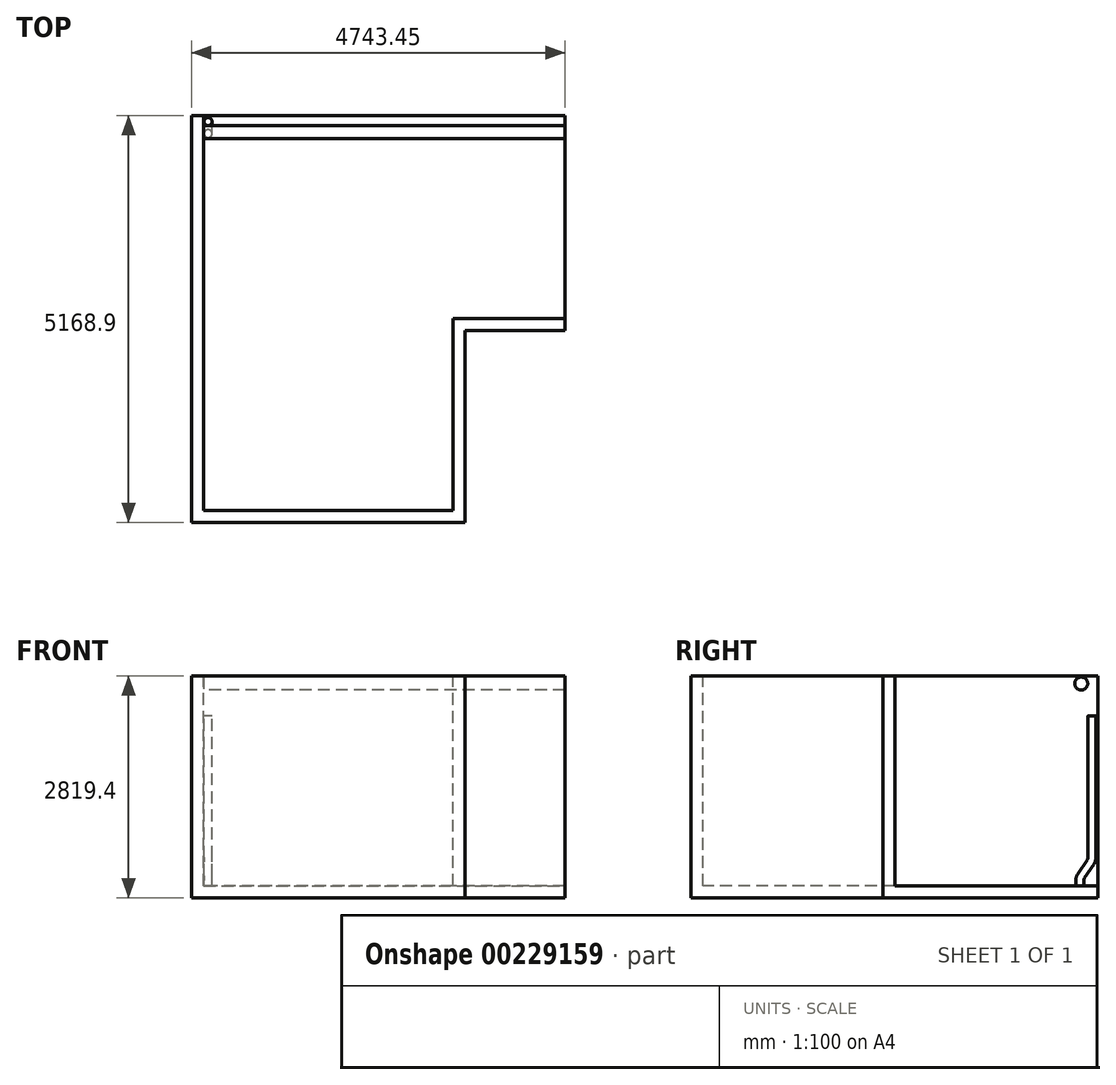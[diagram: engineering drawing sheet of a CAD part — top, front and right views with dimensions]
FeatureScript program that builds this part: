
annotation { "Feature Type Name" : "Feature", "Feature Type Description" : "" }
export const myFeature = defineFeature(function(context is Context, id is Id, definition is map)
    precondition{}
    {
        {
            var Q0;
            Q0=qCreatedBy(makeId("Top.planeOp"),FACE);
            var sketch = newSketch(context, id + "F0", { "sketchPlane" : qUnion([Q0])});
            skLineSegment(sketch, "E0", {"start": v(0, 0) * mm, "end": v(4584.7, 0) * mm});
            skLineSegment(sketch, "E1", {"start": v(4584.7, 0) * mm, "end": v(4584.7, -2578.1) * mm});
            skLineSegment(sketch, "E2", {"start": v(4584.7, -2578.1) * mm, "end": v(3162.3, -2578.1) * mm});
            skLineSegment(sketch, "E3", {"start": v(3162.3, -2578.1) * mm, "end": v(3162.3, -5016.5) * mm});
            skLineSegment(sketch, "E4", {"start": v(3162.3, -5016.5) * mm, "end": v(0, -5016.5) * mm});
            skLineSegment(sketch, "E5", {"start": v(0, 0) * mm, "end": v(0, -5016.5) * mm});
            skLineSegment(sketch, "E6", {"start": v(0, 0) * mm, "end": v(0, -228.6) * mm});
            skLineSegment(sketch, "E7", {"start": v(0, -228.6) * mm, "end": v(50.8, -228.6) * mm});
            skCircle(sketch, "E8", {"center": v(50.8, -228.6) * mm, "radius": 50.8 * mm});
            skSolve(sketch);
        }
        {
            var Q0;
            Q0=qCreatedBy(makeId("Right.planeOp"),FACE);
            var sketch = newSketch(context, id + "F1", { "sketchPlane" : qUnion([Q0])});
            skLineSegment(sketch, "E9", {"start": v(0, 0) * mm, "end": v(-228.6, 0) * mm});
            skLineSegment(sketch, "E10", {"start": v(-228.6, 0) * mm, "end": v(-228.6, 70.84) * mm});
            skLineSegment(sketch, "E11", {"start": v(-76.2, 360.96) * mm, "end": v(-76.2, 2159) * mm});
            skLineSegment(sketch, "E12", {"start": v(-93.26, 304.6) * mm, "end": v(-211.54, 127.2) * mm});
            skPoint(sketch, "E13.visualSharp", {"position": v(-228.6, 101.6) * mm});
            skArc(sketch, "E13.filletArc", {"start": v(-211.54, 127.2) * mm, "mid": v(-224.24, 100.28) * mm, "end": v(-228.6, 70.84) * mm});
            skPoint(sketch, "E14.visualSharp", {"position": v(-76.2, 330.2) * mm});
            skArc(sketch, "E14.filletArc", {"start": v(-93.26, 304.6) * mm, "mid": v(-80.56, 331.52) * mm, "end": v(-76.2, 360.96) * mm});
            skCircle(sketch, "E15", {"center": v(-211.54, 2570.42) * mm, "radius": 82.55 * mm});
            skLineSegment(sketch, "E16", {"start": v(-228.6, 0) * mm, "end": v(-211.54, 2570.42) * mm});
            skSolve(sketch);
        }
        {
            var Q0;
            Q0=makeQuery(id+"F0.imprint","IMPRINT",FACE,{"disambiguationData":[TD([[makeQuery(id+"F0.imprint","IMPRINT",EDGE,{"derivedFrom":sQuery(id+"F0.wireOp",EDGE,"E8")}),1.0]])]});
            var Q1;
            Q1=sQuery(id+"F1.wireOp",EDGE,"E10");
            var Q2;
            Q2=sQuery(id+"F1.wireOp",EDGE,"E13.filletArc");
            var Q3;
            Q3=sQuery(id+"F1.wireOp",EDGE,"E12");
            var Q4;
            Q4=sQuery(id+"F1.wireOp",EDGE,"E14.filletArc");
            var Q5;
            Q5=sQuery(id+"F1.wireOp",EDGE,"E11");
            sweep(context, id + "F2", {"profiles" : qUnion([Q0]), "path" : qUnion([Q1, Q2, Q3, Q4, Q5])});
        }
        {
            var Q0;
            Q0=makeQuery(id+"F0.imprint","IMPRINT",FACE,{"disambiguationData":[TD([[makeQuery(id+"F0.imprint","IMPRINT",EDGE,{"derivedFrom":sQuery(id+"F0.wireOp",EDGE,"E8")}),1.0]])]});
            var Q1;
            Q1=makeQuery(id+"F0.imprint","IMPRINT",FACE,{"disambiguationData":[TD([[makeQuery(id+"F0.imprint","IMPRINT",EDGE,{"derivedFrom":sQuery(id+"F0.wireOp",EDGE,"E0")}),-1.0]])]});
            extrude(context, id + "F3", {"entities" : qUnion([Q0, Q1]), "operationType" : NewBodyOperationType.ADD, "oppositeDirection" : true, "depth" : 152.4 * mm});
        }
        {
            var Q0;
            Q0=makeQuery(id+"F3.opExtrude","SWEPT_FACE",FACE,{"disambiguationData":[OSD([sQuery(id+"F0.wireOp",EDGE,"E5"),sQuery(id+"F0.wireOp",EDGE,"E6")])]});
            extrude(context, id + "F4", {"entities" : qUnion([Q0]), "operationType" : NewBodyOperationType.ADD, "depth" : 6.35 * mm});
        }
        {
            var Q0;
            Q0=makeQuery(id+"F4.opExtrude","CAP_FACE",FACE,{"disambiguationData":[OSD([sQuery(id+"F0.wireOp",EDGE,"E5"),sQuery(id+"F0.wireOp",EDGE,"E6")])],"isStart":false});
            extrude(context, id + "F5", {"entities" : qUnion([Q0]), "depth" : 152.4 * mm});
        }
        {
            var Q0;
            {var subQ1=sQuery(id+"F0.wireOp",EDGE,"E6");var subQ2=sQuery(id+"F0.wireOp",EDGE,"E5");var subQ3=sQuery(id+"F0.wireOp",EDGE,"E4");var subQ4=sQuery(id+"F0.wireOp",EDGE,"E0");var subQ7=makeQuery(id+"F3.opExtrude","CAP_EDGE",EDGE,{"disambiguationData":[OSD([subQ2,subQ1])],"isStart":true});Q0=makeQuery(id+"F5.opExtrude","SWEPT_FACE",FACE,{"disambiguationData":[OSD([subQ2,subQ1]),TDD([makeQuery(id+"F4.opExtrude","CAP_EDGE",EDGE,{"disambiguationData":[OSD([subQ2,subQ1]),TDD([makeQuery(id+"F3.boolean.opBoolean","SPLIT",EDGE,{"disambiguationData":[TD([makeQuery(id+"F3.opExtrude","SWEPT_FACE",FACE,{"disambiguationData":[OSD([subQ4])]})])],"derivedFrom":subQ7}),makeQuery(id+"F3.boolean.opBoolean","SPLIT",EDGE,{"disambiguationData":[TD([makeQuery(id+"F3.opExtrude","SWEPT_FACE",FACE,{"disambiguationData":[OSD([subQ3])]})])],"derivedFrom":subQ7})])],"isStart":false})])]});}
            extrude(context, id + "F6", {"entities" : qUnion([Q0]), "operationType" : NewBodyOperationType.ADD, "depth" : 2667 * mm});
        }
        {
            var Q0;
            Q0=makeQuery(id+"F1.imprint","IMPRINT",FACE,{"disambiguationData":[TD([[makeQuery(id+"F1.imprint","IMPRINT",EDGE,{"derivedFrom":sQuery(id+"F1.wireOp",EDGE,"E15")}),1.0]])]});
            var Q1;
            Q1=sQuery(id+"F0.wireOp",VERTEX,"E1.start");
            extrude(context, id + "F7", {"entities" : qUnion([Q0]), "endBound" : BoundingType.UP_TO_VERTEX, "endBoundEntityVertex" : qUnion([Q1]), "depth" : 6477 * mm});
        }
        {
            var Q0;
            Q0=makeQuery(id+"F1.imprint","IMPRINT",FACE,{"disambiguationData":[TD([[makeQuery(id+"F1.imprint","IMPRINT",EDGE,{"derivedFrom":sQuery(id+"F1.wireOp",EDGE,"E15")}),1.0]])]});
            extrude(context, id + "F8", {"entities" : qUnion([Q0]), "operationType" : NewBodyOperationType.ADD, "oppositeDirection" : true, "depth" : 152.4 * mm});
        }
        {
            var Q0;
            {var subQ0=sQuery(id+"F0.wireOp",EDGE,"E5");var subQ1=sQuery(id+"F0.wireOp",EDGE,"E4");Q0=makeQuery(id+"F6.boolean.opBoolean","MERGE",FACE,{"derivedFrom":[makeQuery(id+"F4.boolean.opBoolean","MERGE",FACE,{"derivedFrom":[makeQuery(id+"F3.opExtrude","SWEPT_FACE",FACE,{"disambiguationData":[OSD([subQ1])]}),makeQuery(id+"F4.opExtrude","SWEPT_FACE",FACE,{"disambiguationData":[OSD([subQ1,subQ0])]})]}),makeQuery(id+"F5.opExtrude","SWEPT_FACE",FACE,{"disambiguationData":[OSD([subQ1,subQ0])]}),makeQuery(id+"F6.opExtrude","SWEPT_FACE",FACE,{"disambiguationData":[OSD([subQ1,subQ0])]})]});}
            extrude(context, id + "F9", {"entities" : qUnion([Q0]), "depth" : 152.4 * mm});
        }
        {
            var Q0;
            {var subQ0=sQuery(id+"F0.wireOp",EDGE,"E5");var subQ1=sQuery(id+"F0.wireOp",EDGE,"E4");Q0=makeQuery(id+"F9.opExtrude","SWEPT_FACE",FACE,{"disambiguationData":[OSD([subQ1,subQ0]),TDD([makeQuery(id+"F4.boolean.opBoolean","MERGE",EDGE,{"derivedFrom":[makeQuery(id+"F3.opExtrude","CAP_EDGE",EDGE,{"disambiguationData":[OSD([subQ1])],"isStart":true}),makeQuery(id+"F4.opExtrude","SWEPT_EDGE",EDGE,{"disambiguationData":[OSD([subQ1,subQ0]),TDD([makeQuery(id+"F3.opExtrude","CAP_VERTEX",VERTEX,{"disambiguationData":[OSD([subQ1,subQ0])],"isStart":true})])]})]})])]});}
            var Q1;
            {var subQ0=sQuery(id+"F0.wireOp",EDGE,"E5");var subQ1=sQuery(id+"F0.wireOp",EDGE,"E4");Q1=makeQuery(id+"F9.opExtrude","SWEPT_FACE",FACE,{"disambiguationData":[OSD([subQ1,subQ0]),TDD([makeQuery(id+"F6.opExtrude","CAP_EDGE",EDGE,{"disambiguationData":[OSD([subQ1,subQ0])],"isStart":false})])]});}
            extrude(context, id + "F10", {"entities" : qUnion([Q0]), "operationType" : NewBodyOperationType.ADD, "endBound" : BoundingType.UP_TO_SURFACE, "endBoundEntityFace" : qUnion([Q1]), "depth" : 25.4 * mm});
        }
        {
            var Q0;
            {var subQ0=sQuery(id+"F0.wireOp",EDGE,"E4");var subQ1=sQuery(id+"F0.wireOp",EDGE,"E3");Q0=makeQuery(id+"F10.boolean.opBoolean","MERGE",FACE,{"derivedFrom":[makeQuery(id+"F9.opExtrude","SWEPT_FACE",FACE,{"disambiguationData":[OSD([subQ1,subQ0])]}),makeQuery(id+"F10.opExtrude","SWEPT_FACE",FACE,{"disambiguationData":[OSD([subQ1,subQ0])]})]});}
            extrude(context, id + "F11", {"entities" : qUnion([Q0]), "depth" : 152.4 * mm});
        }
        {
            var Q0;
            {var subQ0=sQuery(id+"F0.wireOp",EDGE,"E4");var subQ1=sQuery(id+"F0.wireOp",EDGE,"E3");Q0=makeQuery(id+"F11.opExtrude","SWEPT_FACE",FACE,{"disambiguationData":[OSD([subQ1,subQ0]),TDD([makeQuery(id+"F10.boolean.opBoolean","MERGE",EDGE,{"derivedFrom":[makeQuery(id+"F9.opExtrude","CAP_EDGE",EDGE,{"disambiguationData":[OSD([subQ1,subQ0])],"isStart":true}),makeQuery(id+"F10.opExtrude","SWEPT_EDGE",EDGE,{"disambiguationData":[OSD([subQ1,subQ0]),TDD([makeQuery(id+"F9.opExtrude","CAP_VERTEX",VERTEX,{"disambiguationData":[OSD([subQ1,subQ0]),TDD([makeQuery(id+"F3.opExtrude","CAP_VERTEX",VERTEX,{"disambiguationData":[OSD([subQ1,subQ0])],"isStart":true})])],"isStart":true})])]})]})])]});}
            var Q1;
            Q1=makeQuery(id+"F3.opExtrude","SWEPT_FACE",FACE,{"disambiguationData":[OSD([sQuery(id+"F0.wireOp",EDGE,"E2")])]});
            extrude(context, id + "F12", {"entities" : qUnion([Q0]), "operationType" : NewBodyOperationType.ADD, "endBound" : BoundingType.UP_TO_SURFACE, "endBoundEntityFace" : qUnion([Q1]), "depth" : 25.4 * mm});
        }
        {
            var Q0;
            Q0=makeQuery(id+"F3.opExtrude","SWEPT_FACE",FACE,{"disambiguationData":[OSD([sQuery(id+"F0.wireOp",EDGE,"E2")])]});
            extrude(context, id + "F13", {"entities" : qUnion([Q0]), "depth" : 152.4 * mm});
        }
        {
            var Q0;
            {var subQ5=sQuery(id+"F0.wireOp",EDGE,"E2");var subQ6=sQuery(id+"F0.wireOp",EDGE,"E1");Q0=makeQuery(id+"F13.opExtrude","SWEPT_FACE",FACE,{"disambiguationData":[OSD([subQ5]),TDD([makeQuery(id+"F12.boolean.opBoolean","SPLIT",EDGE,{"disambiguationData":[TD([makeQuery(id+"F3.opExtrude","SWEPT_FACE",FACE,{"disambiguationData":[OSD([subQ6])]})])],"derivedFrom":makeQuery(id+"F3.opExtrude","CAP_EDGE",EDGE,{"disambiguationData":[OSD([subQ5])],"isStart":true})})])]});}
            var Q1;
            {var subQ0=sQuery(id+"F0.wireOp",EDGE,"E5");var subQ1=sQuery(id+"F0.wireOp",EDGE,"E4");var subQ2=sQuery(id+"F0.wireOp",EDGE,"E3");Q1=makeQuery(id+"F12.boolean.opBoolean","MERGE",FACE,{"derivedFrom":[makeQuery(id+"F6.opExtrude","CAP_FACE",FACE,{"disambiguationData":[OSD([subQ0,sQuery(id+"F0.wireOp",EDGE,"E6")])],"isStart":false}),makeQuery(id+"F10.boolean.opBoolean","MERGE",FACE,{"derivedFrom":[makeQuery(id+"F9.opExtrude","SWEPT_FACE",FACE,{"disambiguationData":[OSD([subQ1,subQ0]),TDD([makeQuery(id+"F6.opExtrude","CAP_EDGE",EDGE,{"disambiguationData":[OSD([subQ1,subQ0])],"isStart":false})])]}),makeQuery(id+"F10.opExtrude","CAP_FACE",FACE,{"disambiguationData":[OSD([subQ1,subQ0])],"isStart":false})]}),makeQuery(id+"F11.opExtrude","SWEPT_FACE",FACE,{"disambiguationData":[OSD([subQ2,subQ1,subQ0])]}),makeQuery(id+"F12.opExtrude","SWEPT_FACE",FACE,{"disambiguationData":[OSD([subQ2,subQ1,subQ0])]})]});}
            extrude(context, id + "F14", {"entities" : qUnion([Q0]), "operationType" : NewBodyOperationType.ADD, "endBound" : BoundingType.UP_TO_SURFACE, "endBoundEntityFace" : qUnion([Q1]), "depth" : 25.4 * mm});
        }
    });
